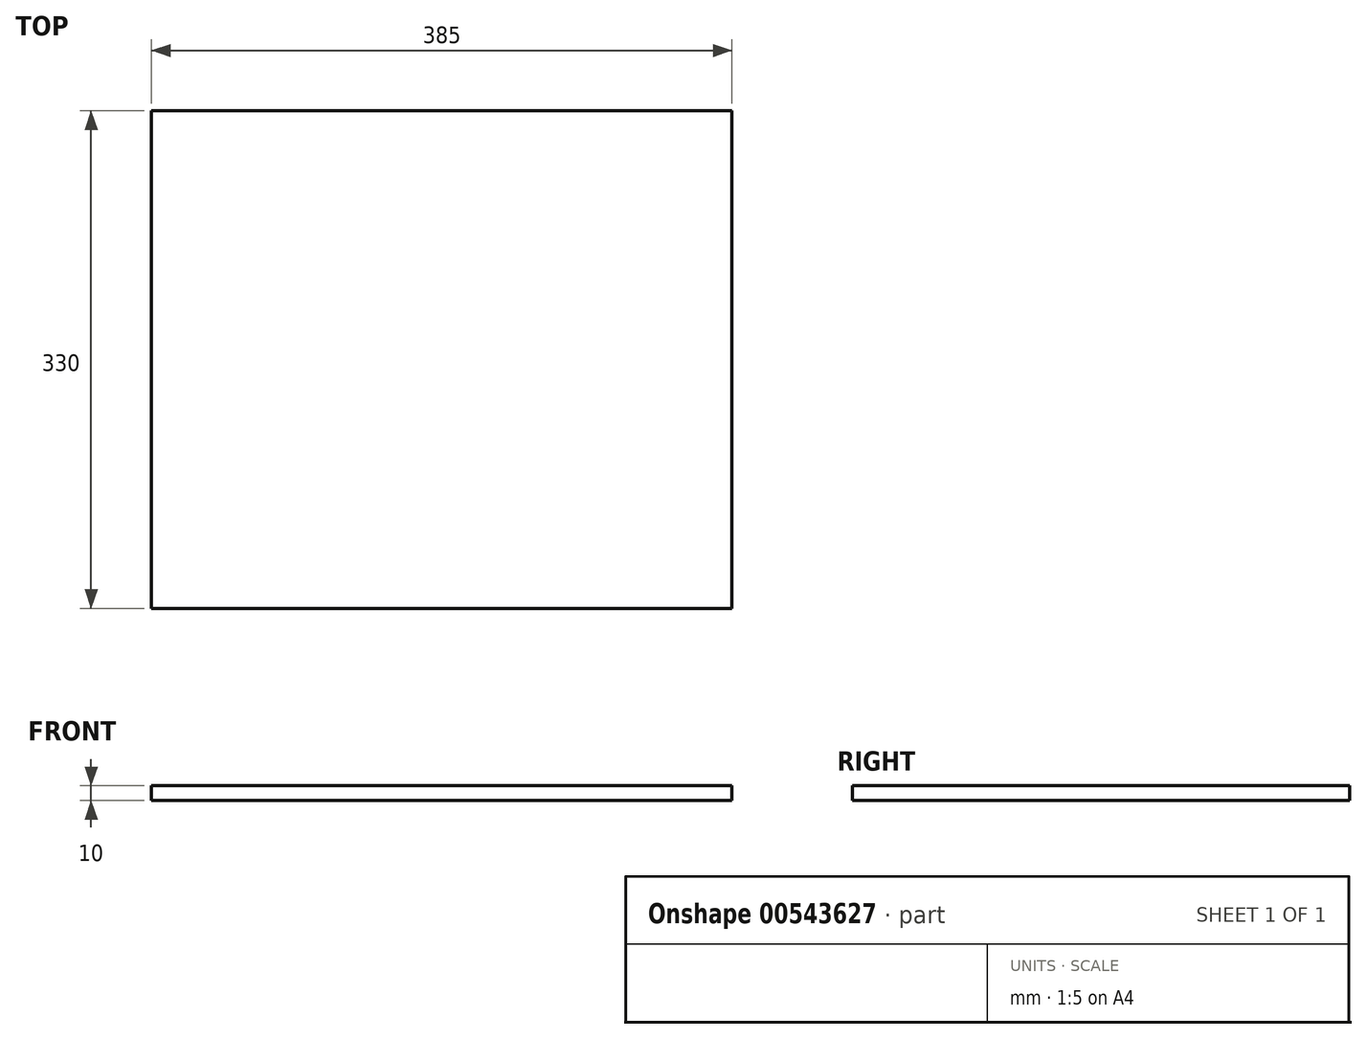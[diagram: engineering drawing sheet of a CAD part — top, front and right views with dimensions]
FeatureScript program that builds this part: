
annotation { "Feature Type Name" : "Feature", "Feature Type Description" : "" }
export const myFeature = defineFeature(function(context is Context, id is Id, definition is map)
    precondition{}
    {
        {
            var Q0;
            Q0=qCreatedBy(makeId("Top.planeOp"),FACE);
            var sketch = newSketch(context, id + "F0", { "sketchPlane" : qUnion([Q0])});
            skLineSegment(sketch, "E0.bottom", {"start": v(-70.96, 65.05) * mm, "end": v(314.04, 65.05) * mm});
            skLineSegment(sketch, "E0.top", {"start": v(-70.96, -264.95) * mm, "end": v(314.04, -264.95) * mm});
            skLineSegment(sketch, "E0.left", {"start": v(-70.96, 65.05) * mm, "end": v(-70.96, -264.95) * mm});
            skLineSegment(sketch, "E0.right", {"start": v(314.04, 65.05) * mm, "end": v(314.04, -264.95) * mm});
            skSolve(sketch);
        }
        {
            var Q0;
            Q0=qSketchRegion(id+"F0",true);
            extrude(context, id + "F1", {"entities" : qUnion([Q0]), "depth" : 10 * mm});
        }
    });
